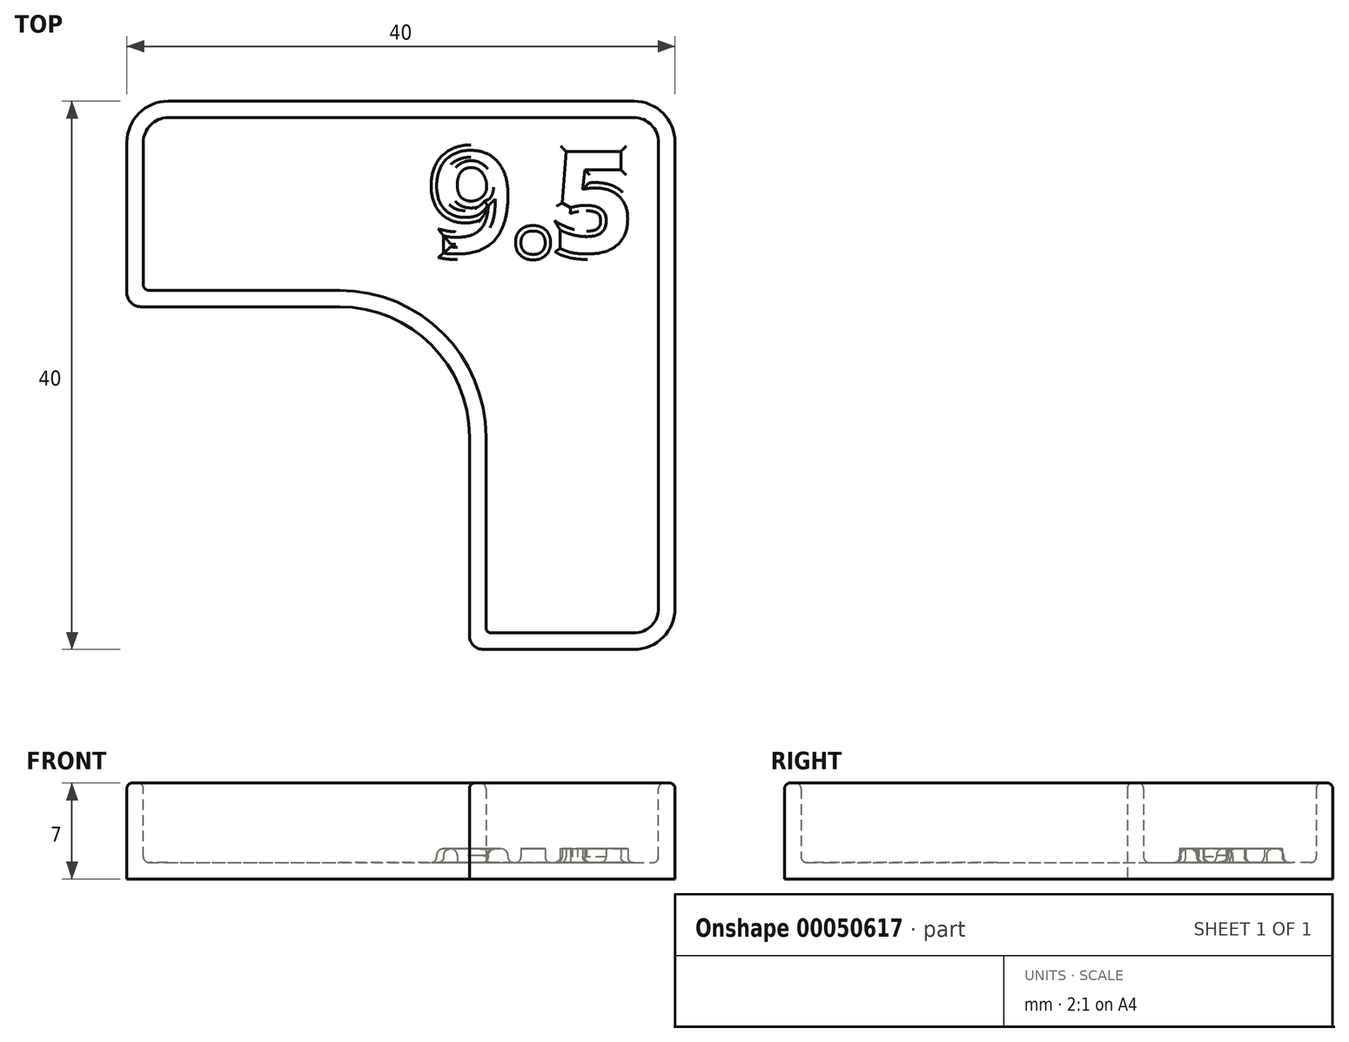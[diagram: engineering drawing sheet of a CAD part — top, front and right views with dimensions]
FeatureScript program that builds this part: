
annotation { "Feature Type Name" : "Feature", "Feature Type Description" : "" }
export const myFeature = defineFeature(function(context is Context, id is Id, definition is map)
    precondition{}
    {
        {
            var Q0;
            Q0=qCreatedBy(makeId("Top.planeOp"),FACE);
            var sketch = newSketch(context, id + "F0", { "sketchPlane" : qUnion([Q0])});
            skLineSegment(sketch, "E0.bottom", {"start": v(26, 0) * mm, "end": v(37, 0) * mm});
            skLineSegment(sketch, "E0.top", {"start": v(3, 40) * mm, "end": v(37, 40) * mm});
            skLineSegment(sketch, "E0.left", {"start": v(0, 26) * mm, "end": v(0, 37) * mm});
            skLineSegment(sketch, "E0.right", {"start": v(40, 3) * mm, "end": v(40, 37) * mm});
            skLineSegment(sketch, "E1", {"start": v(1, 25) * mm, "end": v(15.5, 25) * mm});
            skPoint(sketch, "E1.endSnap0", {"position": v(0, 25) * mm});
            skLineSegment(sketch, "E2", {"start": v(25, 15.5) * mm, "end": v(25, 1) * mm});
            skPoint(sketch, "E3.orphan", {"position": v(0, 0) * mm});
            skArc(sketch, "E4.filletArc", {"start": v(25, 15.5) * mm, "mid": v(22.22, 22.22) * mm, "end": v(15.5, 25) * mm});
            skPoint(sketch, "E5.visualSharp", {"position": v(0, 40) * mm});
            skArc(sketch, "E5.filletArc", {"start": v(3, 40) * mm, "mid": v(0.88, 39.12) * mm, "end": v(0, 37) * mm});
            skPoint(sketch, "E6.visualSharp", {"position": v(40, 40) * mm});
            skArc(sketch, "E6.filletArc", {"start": v(40, 37) * mm, "mid": v(39.12, 39.12) * mm, "end": v(37, 40) * mm});
            skPoint(sketch, "E7.visualSharp", {"position": v(40, 0) * mm});
            skArc(sketch, "E7.filletArc", {"start": v(37, 0) * mm, "mid": v(39.12, 0.88) * mm, "end": v(40, 3) * mm});
            skArc(sketch, "E8.filletArc", {"start": v(0, 26) * mm, "mid": v(0.3, 25.3) * mm, "end": v(1, 25) * mm});
            skPoint(sketch, "E9.visualSharp", {"position": v(25, 0) * mm});
            skArc(sketch, "E9.filletArc", {"start": v(25, 1) * mm, "mid": v(25.3, 0.3) * mm, "end": v(26, 0) * mm});
            skSolve(sketch);
        }
        {
            var Q0;
            Q0 = qSketchRegion(id + "F0", true);
            extrude(context, id + "F1", {"entities" : qUnion([Q0]), "depth" : 7 * mm});
        }
        {
            var Q0;
            Q0=makeQuery(id+"F1.opExtrude","CAP_FACE",FACE,{"disambiguationData":[OSD([sQuery(id+"F0.wireOp",EDGE,"E0.bottom"),sQuery(id+"F0.wireOp",EDGE,"E0.top"),sQuery(id+"F0.wireOp",EDGE,"E0.left"),sQuery(id+"F0.wireOp",EDGE,"E0.right"),sQuery(id+"F0.wireOp",EDGE,"E1"),sQuery(id+"F0.wireOp",EDGE,"E2"),sQuery(id+"F0.wireOp",EDGE,"E4.filletArc"),sQuery(id+"F0.wireOp",EDGE,"E5.filletArc"),sQuery(id+"F0.wireOp",EDGE,"E6.filletArc"),sQuery(id+"F0.wireOp",EDGE,"E7.filletArc"),sQuery(id+"F0.wireOp",EDGE,"E8.filletArc"),sQuery(id+"F0.wireOp",EDGE,"E9.filletArc")])],"isStart":false});
            shell(context, id + "F2", {"entities" : qUnion([Q0]), "thickness" : 1.2 * mm});
        }
        {
            var Q0;
            Q0=makeQuery(id+"F2.opShell","OFFSET_EDGE",EDGE,{"disambiguationData":[OSD([sQuery(id+"F0.wireOp",EDGE,"E0.left"),sQuery(id+"F0.wireOp",EDGE,"E1"),sQuery(id+"F0.wireOp",EDGE,"E8.filletArc")])]});
            var Q1;
            Q1=makeQuery(id+"F2.opShell","OFFSET_EDGE",EDGE,{"disambiguationData":[OSD([sQuery(id+"F0.wireOp",EDGE,"E0.bottom"),sQuery(id+"F0.wireOp",EDGE,"E2"),sQuery(id+"F0.wireOp",EDGE,"E9.filletArc")])]});
            fillet(context, id + "F3", {"entities" : qUnion([Q0, Q1]), "radius" : .4 * mm, "tangentPropagation" : true, "allowEdgeOverflow" : false});
        }
        {
            var Q0;
            Q0=makeQuery(id+"F1.opExtrude","CAP_FACE",FACE,{"disambiguationData":[OSD([sQuery(id+"F0.wireOp",EDGE,"E0.bottom"),sQuery(id+"F0.wireOp",EDGE,"E0.top"),sQuery(id+"F0.wireOp",EDGE,"E0.left"),sQuery(id+"F0.wireOp",EDGE,"E0.right"),sQuery(id+"F0.wireOp",EDGE,"E1"),sQuery(id+"F0.wireOp",EDGE,"E2"),sQuery(id+"F0.wireOp",EDGE,"E4.filletArc"),sQuery(id+"F0.wireOp",EDGE,"E5.filletArc"),sQuery(id+"F0.wireOp",EDGE,"E6.filletArc"),sQuery(id+"F0.wireOp",EDGE,"E7.filletArc"),sQuery(id+"F0.wireOp",EDGE,"E8.filletArc"),sQuery(id+"F0.wireOp",EDGE,"E9.filletArc")])],"isStart":false});
            fillet(context, id + "F4", {"entities" : qUnion([Q0]), "radius" : .4 * mm, "tangentPropagation" : true, "allowEdgeOverflow" : false});
        }
        {
            var Q0;
            Q0=makeQuery(id+"F2.opShell","OFFSET_FACE",FACE,{"disambiguationData":[OSD([sQuery(id+"F0.wireOp",EDGE,"E0.bottom"),sQuery(id+"F0.wireOp",EDGE,"E0.top"),sQuery(id+"F0.wireOp",EDGE,"E0.left"),sQuery(id+"F0.wireOp",EDGE,"E0.right"),sQuery(id+"F0.wireOp",EDGE,"E1"),sQuery(id+"F0.wireOp",EDGE,"E2"),sQuery(id+"F0.wireOp",EDGE,"E4.filletArc"),sQuery(id+"F0.wireOp",EDGE,"E5.filletArc"),sQuery(id+"F0.wireOp",EDGE,"E6.filletArc"),sQuery(id+"F0.wireOp",EDGE,"E7.filletArc"),sQuery(id+"F0.wireOp",EDGE,"E8.filletArc"),sQuery(id+"F0.wireOp",EDGE,"E9.filletArc")])]});
            var sketch = newSketch(context, id + "F5", { "sketchPlane" : qUnion([Q0])});
            skText(sketch, "E10", { "text": "9.5", "fontName": "OpenSans-Bold.ttf"});
            const initialGuessF5  = {"E10": [0.02227, 0.02895, 1, 0, 0.00744]};
            skSetInitialGuess(sketch, initialGuessF5);
            skSolve(sketch);
        }
        {
            var Q0;
            Q0 = qSketchRegion(id + "F5", true);
            extrude(context, id + "F6", {"entities" : qUnion([Q0]), "operationType" : NewBodyOperationType.ADD, "depth" : 1 * mm});
        }
        {
            var Q0;
            {var subQ0=sQuery(id+"F0.wireOp",EDGE,"E6.filletArc");var subQ1=sQuery(id+"F0.wireOp",EDGE,"E5.filletArc");var subQ2=sQuery(id+"F0.wireOp",EDGE,"E4.filletArc");var subQ3=sQuery(id+"F0.wireOp",EDGE,"E2");var subQ4=sQuery(id+"F0.wireOp",EDGE,"E1");var subQ5=sQuery(id+"F0.wireOp",EDGE,"E0.bottom");var subQ6=sQuery(id+"F0.wireOp",EDGE,"E0.top");var subQ7=sQuery(id+"F0.wireOp",EDGE,"E7.filletArc");var subQ8=sQuery(id+"F0.wireOp",EDGE,"E0.left");var subQ9=sQuery(id+"F0.wireOp",EDGE,"E0.right");var subQ10=sQuery(id+"F0.wireOp",EDGE,"E9.filletArc");var subQ11=sQuery(id+"F0.wireOp",EDGE,"E8.filletArc");Q0=makeQuery(id+"F6.boolean.opBoolean","SPLIT",FACE,{"disambiguationData":[TD([makeQuery(id+"F2.opShell","OFFSET_FACE",FACE,{"disambiguationData":[OSD([subQ5])]})])],"derivedFrom":makeQuery(id+"F2.opShell","OFFSET_FACE",FACE,{"disambiguationData":[OSD([subQ5,subQ6,subQ8,subQ9,subQ4,subQ3,subQ2,subQ1,subQ0,subQ7,subQ11,subQ10])]})});}
            fillet(context, id + "F7", {"entities" : qUnion([Q0]), "radius" : .4 * mm, "tangentPropagation" : true, "allowEdgeOverflow" : false});
        }
        {
            var Q0;
            Q0=makeQuery(id+"F6.opExtrude","CAP_FACE",FACE,{"disambiguationData":[OSD([sQuery(id+"F5.wireOp",EDGE,"E10.sketch_text.stroke-0"),sQuery(id+"F5.wireOp",EDGE,"E10.sketch_text.stroke-1"),sQuery(id+"F5.wireOp",EDGE,"E10.sketch_text.stroke-2"),sQuery(id+"F5.wireOp",EDGE,"E10.sketch_text.stroke-3"),sQuery(id+"F5.wireOp",EDGE,"E10.sketch_text.stroke-4"),sQuery(id+"F5.wireOp",EDGE,"E10.sketch_text.stroke-5"),sQuery(id+"F5.wireOp",EDGE,"E10.sketch_text.stroke-6"),sQuery(id+"F5.wireOp",EDGE,"E10.sketch_text.stroke-7"),sQuery(id+"F5.wireOp",EDGE,"E10.sketch_text.stroke-8"),sQuery(id+"F5.wireOp",EDGE,"E10.sketch_text.stroke-9"),sQuery(id+"F5.wireOp",EDGE,"E10.sketch_text.stroke-10"),sQuery(id+"F5.wireOp",EDGE,"E10.sketch_text.stroke-11"),sQuery(id+"F5.wireOp",EDGE,"E10.sketch_text.stroke-12"),sQuery(id+"F5.wireOp",EDGE,"E10.sketch_text.stroke-13"),sQuery(id+"F5.wireOp",EDGE,"E10.sketch_text.stroke-14"),sQuery(id+"F5.wireOp",EDGE,"E10.sketch_text.stroke-15"),sQuery(id+"F5.wireOp",EDGE,"E10.sketch_text.stroke-16"),sQuery(id+"F5.wireOp",EDGE,"E10.sketch_text.stroke-17"),sQuery(id+"F5.wireOp",EDGE,"E10.sketch_text.stroke-18"),sQuery(id+"F5.wireOp",EDGE,"E10.sketch_text.stroke-19"),sQuery(id+"F5.wireOp",EDGE,"E10.sketch_text.stroke-20"),sQuery(id+"F5.wireOp",EDGE,"E10.sketch_text.stroke-21"),sQuery(id+"F5.wireOp",EDGE,"E10.sketch_text.stroke-22"),sQuery(id+"F5.wireOp",EDGE,"E10.sketch_text.stroke-23"),sQuery(id+"F5.wireOp",EDGE,"E10.sketch_text.stroke-24"),sQuery(id+"F5.wireOp",EDGE,"E10.sketch_text.stroke-25")])],"isStart":false});
            fillet(context, id + "F8", {"entities" : qUnion([Q0]), "radius" : 0.5 * mm, "tangentPropagation" : true, "allowEdgeOverflow" : false});
        }
    });
